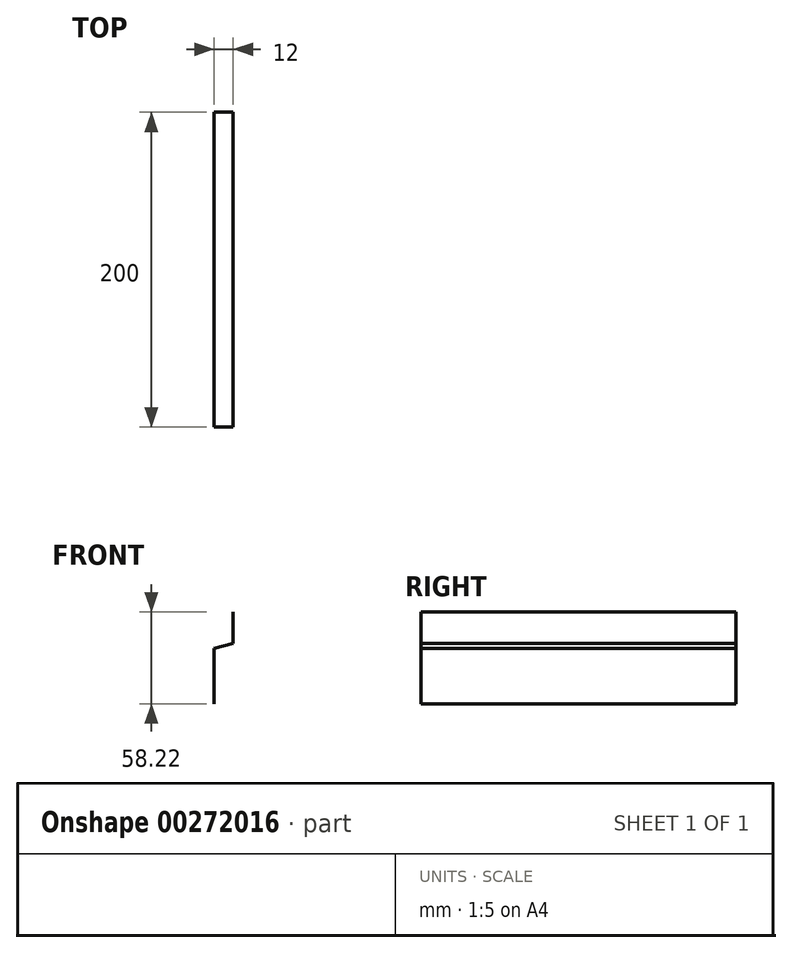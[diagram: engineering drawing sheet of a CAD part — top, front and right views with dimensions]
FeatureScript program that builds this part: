
annotation { "Feature Type Name" : "Feature", "Feature Type Description" : "" }
export const myFeature = defineFeature(function(context is Context, id is Id, definition is map)
    precondition{}
    {
        {
            var Q0;
            Q0=qCreatedBy(makeId("Front.planeOp"),FACE);
            var sketch = newSketch(context, id + "F0", { "sketchPlane" : qUnion([Q0])});
            skLineSegment(sketch, "E0", {"start": v(0, 0) * mm, "end": v(0, -20) * mm});
            skLineSegment(sketch, "E1", {"start": v(0, -20) * mm, "end": v(-12, -23.22) * mm});
            skLineSegment(sketch, "E2", {"start": v(-12, -23.22) * mm, "end": v(-12, -58.22) * mm});
            skSolve(sketch);
        }
        {
            var Q0;
            Q0=sQuery(id+"F0.wireOp",EDGE,"E2");
            var Q1;
            Q1=sQuery(id+"F0.wireOp",EDGE,"E1");
            var Q2;
            Q2=sQuery(id+"F0.wireOp",EDGE,"E0");
            extrude(context, id + "F1", {"bodyType" : ToolBodyType.SURFACE, "surfaceEntities" : qUnion([Q0, Q1, Q2]), "oppositeDirection" : true, "depth" : 200 * mm});
        }
    });
